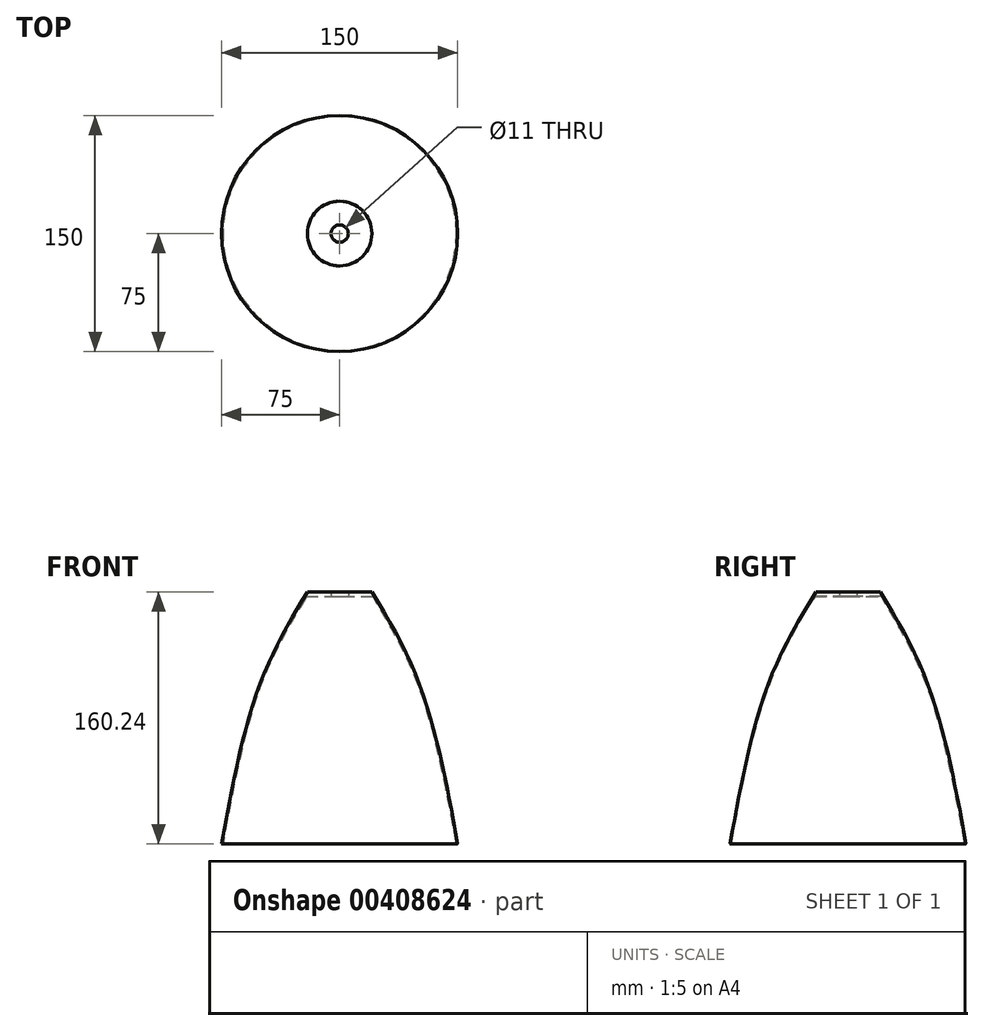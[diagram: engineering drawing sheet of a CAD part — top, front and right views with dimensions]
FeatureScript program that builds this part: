
annotation { "Feature Type Name" : "Feature", "Feature Type Description" : "" }
export const myFeature = defineFeature(function(context is Context, id is Id, definition is map)
    precondition{}
    {
        {
            var Q0;
            Q0=qCreatedBy(makeId("Front.planeOp"),FACE);
            var sketch = newSketch(context, id + "F0", { "sketchPlane" : qUnion([Q0])});
            skLineSegment(sketch, "E0", {"start": v(0, 0) * mm, "end": v(150, 0) * mm, "construction": true});
            skLineSegment(sketch, "E1", {"start": v(150, 0) * mm, "end": v(75, 0) * mm, "construction": true});
            skLineSegment(sketch, "E2", {"start": v(75, 0) * mm, "end": v(75, 160) * mm, "construction": true});
            skLineSegment(sketch, "E3", {"start": v(75, 160) * mm, "end": v(0, 0) * mm, "construction": true});
            skLineSegment(sketch, "E4", {"start": v(75, 160) * mm, "end": v(69.5, 160) * mm, "construction": true});
            skLineSegment(sketch, "E5", {"start": v(69.5, 160) * mm, "end": v(54.5, 160) * mm, "construction": true});
            skLineSegment(sketch, "E6", {"start": v(75, 160) * mm, "end": v(80, 160) * mm, "construction": true});
            skLineSegment(sketch, "E7", {"start": v(80, 160) * mm, "end": v(95, 160) * mm, "construction": true});
            skLineSegment(sketch, "E8", {"start": v(54.5, 160) * mm, "end": v(0, 0) * mm, "construction": true});
            skLineSegment(sketch, "E9", {"start": v(0, 0) * mm, "end": v(0, 160) * mm, "construction": true});
            skLineSegment(sketch, "E10", {"start": v(0, 160) * mm, "end": v(54.5, 160) * mm, "construction": true});
            skFitSpline(sketch, "E11", {"points": [v(0, 0) * mm, v(23.63, 99.38) * mm, v(54.5, 160) * mm], "startDerivative": vector(35.57, 193.23) * mm, "endDerivative": vector(75.77, 124.47) * mm});
            skLineSegment(sketch, "E12", {"start": v(0, 0) * mm, "end": v(3, 0) * mm, "construction": true});
            skLineSegment(sketch, "E13", {"start": v(23.63, 99.38) * mm, "end": v(26.63, 99.38) * mm, "construction": true});
            skLineSegment(sketch, "E14", {"start": v(54.5, 160) * mm, "end": v(57.5, 160) * mm, "construction": true});
            skLineSegment(sketch, "E15", {"start": v(75, 160) * mm, "end": v(75, 155) * mm, "construction": true});
            skLineSegment(sketch, "E16", {"start": v(54.5, 160) * mm, "end": v(69.5, 160) * mm});
            skLineSegment(sketch, "E17", {"start": v(69.5, 160) * mm, "end": v(69.5, 157) * mm});
            skLineSegment(sketch, "E18", {"start": v(0, 0) * mm, "end": v(0.8, 0) * mm, "construction": true});
            skLineSegment(sketch, "E19", {"start": v(23.7, 99.38) * mm, "end": v(24.5, 99.38) * mm, "construction": true});
            skFitSpline(sketch, "E20", {"points": [v(55, 158.75) * mm, v(24.5, 99.38) * mm, v(0.8, 0) * mm], "startDerivative": vector(-73.9, -122.34) * mm, "endDerivative": vector(-35.82, -192.67) * mm});
            skFitSpline(sketch, "E21", {"points": [v(0, 0) * mm, v(0.4, -0.24) * mm, v(0.8, 0) * mm], "startDerivative": vector(0.79, -0.73) * mm, "endDerivative": vector(0.81, 0.72) * mm});
            skLineSegment(sketch, "E22", {"start": v(75, 160) * mm, "end": v(75, 157) * mm, "construction": true});
            skLineSegment(sketch, "E23", {"start": v(69.5, 157) * mm, "end": v(53.93, 157) * mm});
            skLineSegment(sketch, "E24", {"start": v(52.89, 155.27) * mm, "end": v(53.93, 157) * mm});
            skSolve(sketch);
        }
        {
            var Q0;
            Q0 = qSketchRegion(id + "F0", true);
            var Q1;
            Q1=sQuery(id+"F0.wireOp",EDGE,"E2");
            revolve(context, id + "F1", {"entities" : qUnion([Q0]), "axis" : qUnion([Q1]), "revolveType" : RevolveType.FULL});
        }
    });
